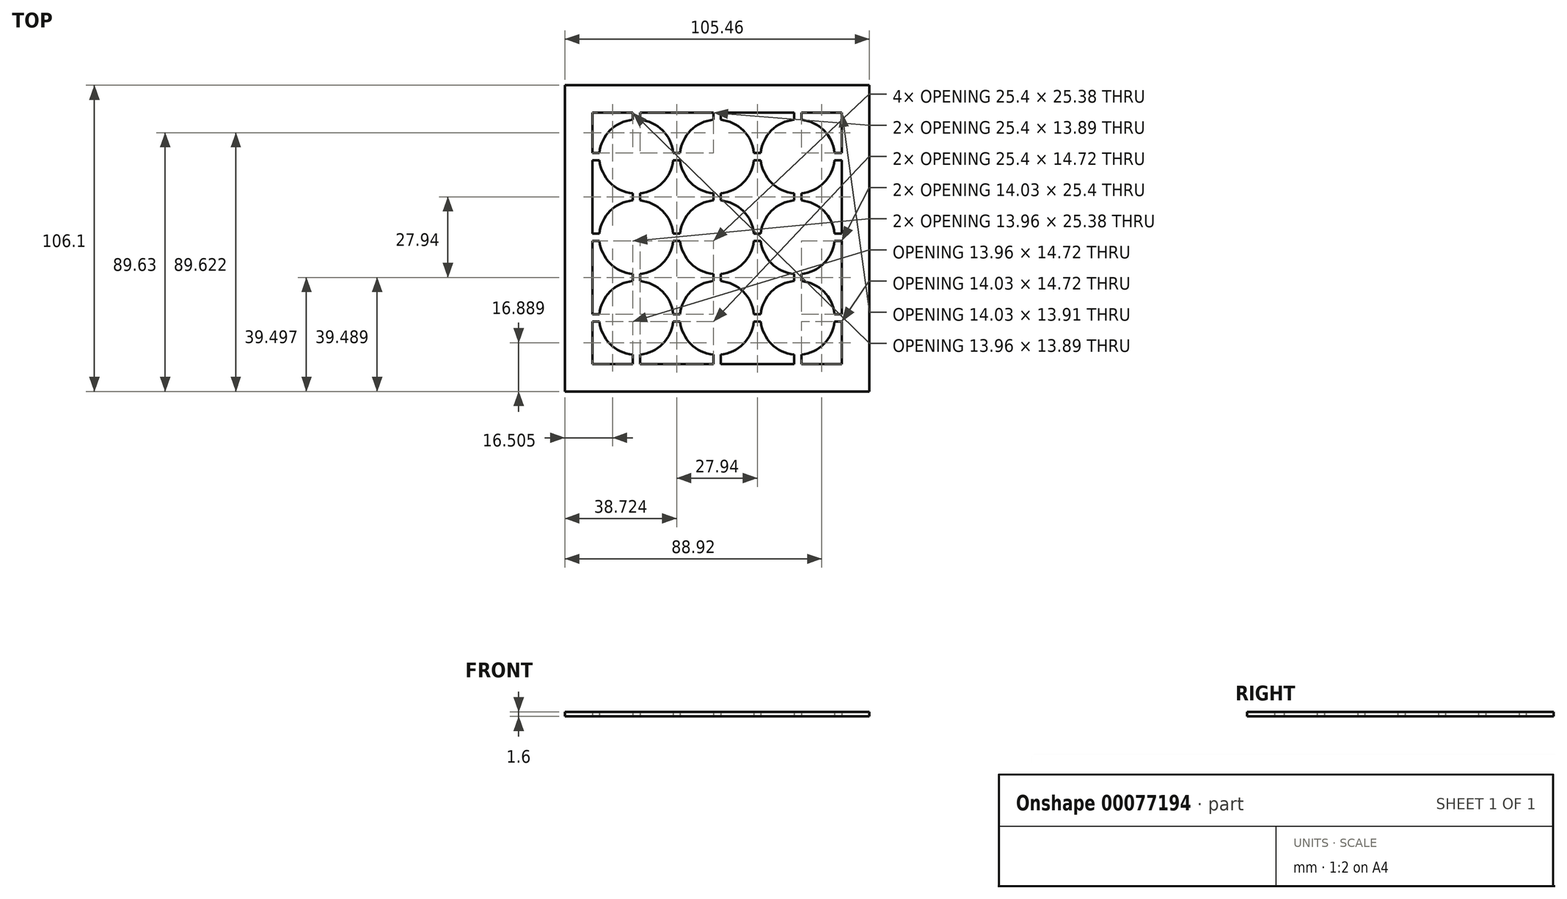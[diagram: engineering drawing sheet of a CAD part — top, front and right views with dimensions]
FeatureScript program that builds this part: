
annotation { "Feature Type Name" : "Feature", "Feature Type Description" : "" }
export const myFeature = defineFeature(function(context is Context, id is Id, definition is map)
    precondition{}
    {
        {
            var Q0;
            Q0=qCreatedBy(makeId("Top.planeOp"),FACE);
            var sketch = newSketch(context, id + "F0", { "sketchPlane" : qUnion([Q0])});
            skArc(sketch, "E0.trimOffspring", {"start": v(220.93, 38.1) * mm, "mid": v(217.23, 45.9) * mm, "end": v(209.43, 49.6) * mm});
            skArc(sketch, "E1.trimOffspring", {"start": v(206.9, 49.6) * mm, "mid": v(199.1, 45.9) * mm, "end": v(195.4, 38.12) * mm});
            skLineSegment(sketch, "E2.bottom", {"start": v(192.94, 38.12) * mm, "end": v(195.4, 38.12) * mm});
            skArc(sketch, "E3.1.1.0", {"start": v(195.4, 35.56) * mm, "mid": v(199.1, 27.76) * mm, "end": v(206.9, 24.07) * mm});
            skLineSegment(sketch, "E4.left", {"start": v(206.9, 20.84) * mm, "end": v(206.9, 24.07) * mm});
            skLineSegment(sketch, "E4.right", {"start": v(209.43, 20.84) * mm, "end": v(209.43, 24.07) * mm});
            skArc(sketch, "E5.trimOffspring", {"start": v(209.43, 24.07) * mm, "mid": v(217.23, 27.76) * mm, "end": v(220.93, 35.56) * mm});
            skArc(sketch, "E6.0.1.0", {"start": v(209.43, 52) * mm, "mid": v(217.23, 55.7) * mm, "end": v(220.93, 63.5) * mm});
            skArc(sketch, "E6.0.1.1", {"start": v(206.9, 77.53) * mm, "mid": v(199.1, 73.85) * mm, "end": v(195.4, 66.06) * mm});
            skArc(sketch, "E6.0.1.2", {"start": v(195.4, 63.5) * mm, "mid": v(199.1, 55.7) * mm, "end": v(206.9, 52) * mm});
            skArc(sketch, "E6.0.1.3", {"start": v(220.93, 66.04) * mm, "mid": v(217.23, 73.84) * mm, "end": v(209.43, 77.53) * mm});
            skLineSegment(sketch, "E6.0.1.4", {"start": v(209.43, 49.6) * mm, "end": v(209.43, 52) * mm});
            skLineSegment(sketch, "E6.0.1.5", {"start": v(206.9, 49.6) * mm, "end": v(206.9, 52) * mm});
            skLineSegment(sketch, "E6.0.1.6", {"start": v(192.94, 66.06) * mm, "end": v(195.4, 66.06) * mm});
            skArc(sketch, "E6.0.2.0", {"start": v(209.43, 79.95) * mm, "mid": v(217.23, 83.64) * mm, "end": v(220.93, 91.44) * mm});
            skArc(sketch, "E6.0.2.1", {"start": v(206.9, 105.47) * mm, "mid": v(199.1, 101.79) * mm, "end": v(195.4, 94) * mm});
            skArc(sketch, "E6.0.2.2", {"start": v(195.4, 91.44) * mm, "mid": v(199.1, 83.64) * mm, "end": v(206.9, 79.95) * mm});
            skArc(sketch, "E6.0.2.3", {"start": v(220.93, 93.98) * mm, "mid": v(217.23, 101.78) * mm, "end": v(209.43, 105.47) * mm});
            skLineSegment(sketch, "E6.0.2.4", {"start": v(209.43, 77.53) * mm, "end": v(209.43, 79.95) * mm});
            skLineSegment(sketch, "E6.0.2.5", {"start": v(206.9, 77.53) * mm, "end": v(206.9, 79.95) * mm});
            skLineSegment(sketch, "E6.0.2.6", {"start": v(192.94, 94) * mm, "end": v(195.4, 94) * mm});
            skLineSegment(sketch, "E6.0.3.4", {"start": v(209.43, 105.47) * mm, "end": v(209.43, 107.89) * mm});
            skLineSegment(sketch, "E6.0.3.5", {"start": v(206.9, 105.47) * mm, "end": v(206.9, 107.89) * mm});
            skArc(sketch, "E6.1.0.0", {"start": v(237.37, 24.07) * mm, "mid": v(245.17, 27.76) * mm, "end": v(248.87, 35.56) * mm});
            skArc(sketch, "E6.1.0.1", {"start": v(234.83, 49.6) * mm, "mid": v(227.04, 45.9) * mm, "end": v(223.34, 38.12) * mm});
            skArc(sketch, "E6.1.0.2", {"start": v(223.34, 35.56) * mm, "mid": v(227.03, 27.76) * mm, "end": v(234.83, 24.07) * mm});
            skArc(sketch, "E6.1.0.3", {"start": v(248.87, 38.1) * mm, "mid": v(245.17, 45.9) * mm, "end": v(237.37, 49.6) * mm});
            skLineSegment(sketch, "E6.1.0.4", {"start": v(237.37, 20.84) * mm, "end": v(237.37, 24.07) * mm});
            skLineSegment(sketch, "E6.1.0.5", {"start": v(234.83, 20.84) * mm, "end": v(234.83, 24.07) * mm});
            skLineSegment(sketch, "E6.1.0.6", {"start": v(220.88, 38.12) * mm, "end": v(223.34, 38.12) * mm});
            skLineSegment(sketch, "E6.1.0.7", {"start": v(220.93, 35.56) * mm, "end": v(223.34, 35.56) * mm});
            skArc(sketch, "E6.1.1.0", {"start": v(237.37, 52) * mm, "mid": v(245.17, 55.7) * mm, "end": v(248.87, 63.5) * mm});
            skArc(sketch, "E6.1.1.1", {"start": v(234.83, 77.53) * mm, "mid": v(227.04, 73.85) * mm, "end": v(223.34, 66.06) * mm});
            skArc(sketch, "E6.1.1.2", {"start": v(223.34, 63.5) * mm, "mid": v(227.03, 55.7) * mm, "end": v(234.83, 52) * mm});
            skArc(sketch, "E6.1.1.3", {"start": v(248.87, 66.04) * mm, "mid": v(245.17, 73.84) * mm, "end": v(237.37, 77.53) * mm});
            skLineSegment(sketch, "E6.1.1.4", {"start": v(237.37, 49.6) * mm, "end": v(237.37, 52) * mm});
            skLineSegment(sketch, "E6.1.1.5", {"start": v(234.83, 49.6) * mm, "end": v(234.83, 52) * mm});
            skLineSegment(sketch, "E6.1.1.6", {"start": v(220.88, 66.06) * mm, "end": v(223.34, 66.06) * mm});
            skLineSegment(sketch, "E6.1.1.7", {"start": v(220.93, 63.5) * mm, "end": v(223.34, 63.5) * mm});
            skArc(sketch, "E6.1.2.0", {"start": v(237.37, 79.95) * mm, "mid": v(245.17, 83.64) * mm, "end": v(248.87, 91.44) * mm});
            skArc(sketch, "E6.1.2.1", {"start": v(234.83, 105.47) * mm, "mid": v(227.04, 101.79) * mm, "end": v(223.34, 94) * mm});
            skArc(sketch, "E6.1.2.2", {"start": v(223.34, 91.44) * mm, "mid": v(227.03, 83.64) * mm, "end": v(234.83, 79.95) * mm});
            skArc(sketch, "E6.1.2.3", {"start": v(248.87, 93.98) * mm, "mid": v(245.17, 101.78) * mm, "end": v(237.37, 105.47) * mm});
            skLineSegment(sketch, "E6.1.2.4", {"start": v(237.37, 77.53) * mm, "end": v(237.37, 79.95) * mm});
            skLineSegment(sketch, "E6.1.2.5", {"start": v(234.83, 77.53) * mm, "end": v(234.83, 79.95) * mm});
            skLineSegment(sketch, "E6.1.2.6", {"start": v(220.88, 94) * mm, "end": v(223.34, 94) * mm});
            skLineSegment(sketch, "E6.1.2.7", {"start": v(220.93, 91.44) * mm, "end": v(223.34, 91.44) * mm});
            skLineSegment(sketch, "E6.1.3.4", {"start": v(237.37, 105.47) * mm, "end": v(237.37, 107.89) * mm});
            skLineSegment(sketch, "E6.1.3.5", {"start": v(234.83, 105.47) * mm, "end": v(234.83, 107.89) * mm});
            skArc(sketch, "E6.2.0.0", {"start": v(265.31, 24.07) * mm, "mid": v(273.11, 27.76) * mm, "end": v(276.8, 35.56) * mm});
            skArc(sketch, "E6.2.0.1", {"start": v(262.77, 49.6) * mm, "mid": v(254.98, 45.9) * mm, "end": v(251.28, 38.12) * mm});
            skArc(sketch, "E6.2.0.2", {"start": v(251.28, 35.56) * mm, "mid": v(254.97, 27.76) * mm, "end": v(262.77, 24.07) * mm});
            skArc(sketch, "E6.2.0.3", {"start": v(276.8, 38.1) * mm, "mid": v(273.11, 45.9) * mm, "end": v(265.31, 49.6) * mm});
            skLineSegment(sketch, "E6.2.0.4", {"start": v(265.31, 20.84) * mm, "end": v(265.31, 24.07) * mm});
            skLineSegment(sketch, "E6.2.0.5", {"start": v(262.77, 20.84) * mm, "end": v(262.77, 24.07) * mm});
            skLineSegment(sketch, "E6.2.0.6", {"start": v(248.82, 38.12) * mm, "end": v(251.28, 38.12) * mm});
            skLineSegment(sketch, "E6.2.0.7", {"start": v(248.87, 35.56) * mm, "end": v(251.28, 35.56) * mm});
            skArc(sketch, "E6.2.1.0", {"start": v(265.31, 52) * mm, "mid": v(273.11, 55.7) * mm, "end": v(276.8, 63.5) * mm});
            skArc(sketch, "E6.2.1.1", {"start": v(262.77, 77.53) * mm, "mid": v(254.98, 73.85) * mm, "end": v(251.28, 66.06) * mm});
            skArc(sketch, "E6.2.1.2", {"start": v(251.28, 63.5) * mm, "mid": v(254.97, 55.7) * mm, "end": v(262.77, 52) * mm});
            skArc(sketch, "E6.2.1.3", {"start": v(276.8, 66.04) * mm, "mid": v(273.11, 73.84) * mm, "end": v(265.31, 77.53) * mm});
            skLineSegment(sketch, "E6.2.1.4", {"start": v(265.31, 49.6) * mm, "end": v(265.31, 52) * mm});
            skLineSegment(sketch, "E6.2.1.5", {"start": v(262.77, 49.6) * mm, "end": v(262.77, 52) * mm});
            skLineSegment(sketch, "E6.2.1.6", {"start": v(248.82, 66.06) * mm, "end": v(251.28, 66.06) * mm});
            skLineSegment(sketch, "E6.2.1.7", {"start": v(248.87, 63.5) * mm, "end": v(251.28, 63.5) * mm});
            skArc(sketch, "E6.2.2.0", {"start": v(265.31, 79.95) * mm, "mid": v(273.11, 83.64) * mm, "end": v(276.8, 91.44) * mm});
            skArc(sketch, "E6.2.2.1", {"start": v(262.77, 105.47) * mm, "mid": v(254.98, 101.79) * mm, "end": v(251.28, 94) * mm});
            skArc(sketch, "E6.2.2.2", {"start": v(251.28, 91.44) * mm, "mid": v(254.97, 83.64) * mm, "end": v(262.77, 79.95) * mm});
            skArc(sketch, "E6.2.2.3", {"start": v(276.8, 93.98) * mm, "mid": v(273.11, 101.78) * mm, "end": v(265.31, 105.47) * mm});
            skLineSegment(sketch, "E6.2.2.4", {"start": v(265.31, 77.53) * mm, "end": v(265.31, 79.95) * mm});
            skLineSegment(sketch, "E6.2.2.5", {"start": v(262.77, 77.53) * mm, "end": v(262.77, 79.95) * mm});
            skLineSegment(sketch, "E6.2.2.6", {"start": v(248.82, 94) * mm, "end": v(251.28, 94) * mm});
            skLineSegment(sketch, "E6.2.2.7", {"start": v(248.87, 91.44) * mm, "end": v(251.28, 91.44) * mm});
            skLineSegment(sketch, "E6.2.3.4", {"start": v(265.31, 105.47) * mm, "end": v(265.31, 107.89) * mm});
            skLineSegment(sketch, "E6.2.3.5", {"start": v(262.77, 105.47) * mm, "end": v(262.77, 107.89) * mm});
            skLineSegment(sketch, "E6.direction1", {"start": v(209.43, 24.07) * mm, "end": v(237.37, 24.07) * mm, "construction": true});
            skLineSegment(sketch, "E6.direction2", {"start": v(209.43, 24.07) * mm, "end": v(209.43, 52) * mm, "construction": true});
            skLineSegment(sketch, "E7.bottom", {"start": v(192.94, 20.84) * mm, "end": v(206.9, 20.84) * mm});
            skLineSegment(sketch, "E7.left", {"start": v(192.94, 20.84) * mm, "end": v(192.94, 35.56) * mm});
            skLineSegment(sketch, "E8.bottom", {"start": v(183.41, 117.41) * mm, "end": v(288.87, 117.41) * mm});
            skLineSegment(sketch, "E8.top", {"start": v(183.41, 11.31) * mm, "end": v(288.87, 11.31) * mm});
            skLineSegment(sketch, "E8.left", {"start": v(183.41, 117.41) * mm, "end": v(183.41, 11.31) * mm});
            skLineSegment(sketch, "E8.right", {"start": v(288.87, 117.41) * mm, "end": v(288.87, 11.31) * mm});
            skLineSegment(sketch, "E9.trimOffspring", {"start": v(265.31, 20.84) * mm, "end": v(279.35, 20.84) * mm});
            skLineSegment(sketch, "E10.trimOffspring", {"start": v(237.37, 20.84) * mm, "end": v(262.77, 20.84) * mm});
            skLineSegment(sketch, "E11.trimOffspring", {"start": v(209.43, 20.84) * mm, "end": v(234.83, 20.84) * mm});
            skLineSegment(sketch, "E12", {"start": v(195.4, 35.56) * mm, "end": v(192.94, 35.56) * mm});
            skLineSegment(sketch, "E13.trimOffspring", {"start": v(192.94, 38.12) * mm, "end": v(192.94, 63.5) * mm});
            skLineSegment(sketch, "E14", {"start": v(195.4, 63.5) * mm, "end": v(192.94, 63.5) * mm});
            skLineSegment(sketch, "E15.trimOffspring", {"start": v(192.94, 66.06) * mm, "end": v(192.94, 91.44) * mm});
            skLineSegment(sketch, "E16", {"start": v(195.4, 91.44) * mm, "end": v(192.94, 91.44) * mm});
            skLineSegment(sketch, "E17.trimOffspring", {"start": v(192.94, 94) * mm, "end": v(192.94, 107.89) * mm});
            skLineSegment(sketch, "E18", {"start": v(276.8, 35.56) * mm, "end": v(279.35, 35.56) * mm});
            skLineSegment(sketch, "E19", {"start": v(279.35, 20.84) * mm, "end": v(279.35, 35.56) * mm});
            skLineSegment(sketch, "E20", {"start": v(279.35, 107.89) * mm, "end": v(265.31, 107.89) * mm});
            skLineSegment(sketch, "E21", {"start": v(276.8, 93.98) * mm, "end": v(279.35, 93.98) * mm});
            skLineSegment(sketch, "E22", {"start": v(276.8, 91.44) * mm, "end": v(279.35, 91.44) * mm});
            skLineSegment(sketch, "E23", {"start": v(276.8, 66.04) * mm, "end": v(279.35, 66.04) * mm});
            skLineSegment(sketch, "E24", {"start": v(276.8, 63.5) * mm, "end": v(279.35, 63.5) * mm});
            skLineSegment(sketch, "E25", {"start": v(276.8, 38.1) * mm, "end": v(279.35, 38.1) * mm});
            skLineSegment(sketch, "E26.trimOffspring", {"start": v(279.35, 93.98) * mm, "end": v(279.35, 107.89) * mm});
            skLineSegment(sketch, "E27.trimOffspring", {"start": v(279.35, 66.04) * mm, "end": v(279.35, 91.44) * mm});
            skLineSegment(sketch, "E28.trimOffspring", {"start": v(279.35, 38.1) * mm, "end": v(279.35, 63.5) * mm});
            skLineSegment(sketch, "E29.trimOffspring", {"start": v(206.9, 107.89) * mm, "end": v(192.94, 107.89) * mm});
            skLineSegment(sketch, "E30.trimOffspring", {"start": v(234.83, 107.89) * mm, "end": v(209.43, 107.89) * mm});
            skLineSegment(sketch, "E31.trimOffspring", {"start": v(262.77, 107.89) * mm, "end": v(237.37, 107.89) * mm});
            skSolve(sketch);
        }
        {
            var Q0;
            Q0=makeQuery(id+"F0.imprint","IMPRINT",FACE,{"disambiguationData":[TD([[makeQuery(id+"F0.imprint","IMPRINT",EDGE,{"derivedFrom":sQuery(id+"F0.wireOp",EDGE,"E1.trimOffspring")}),1.0]])]});
            extrude(context, id + "F1", {"entities" : qUnion([Q0]), "depth" : 1.6 * mm});
        }
    });
